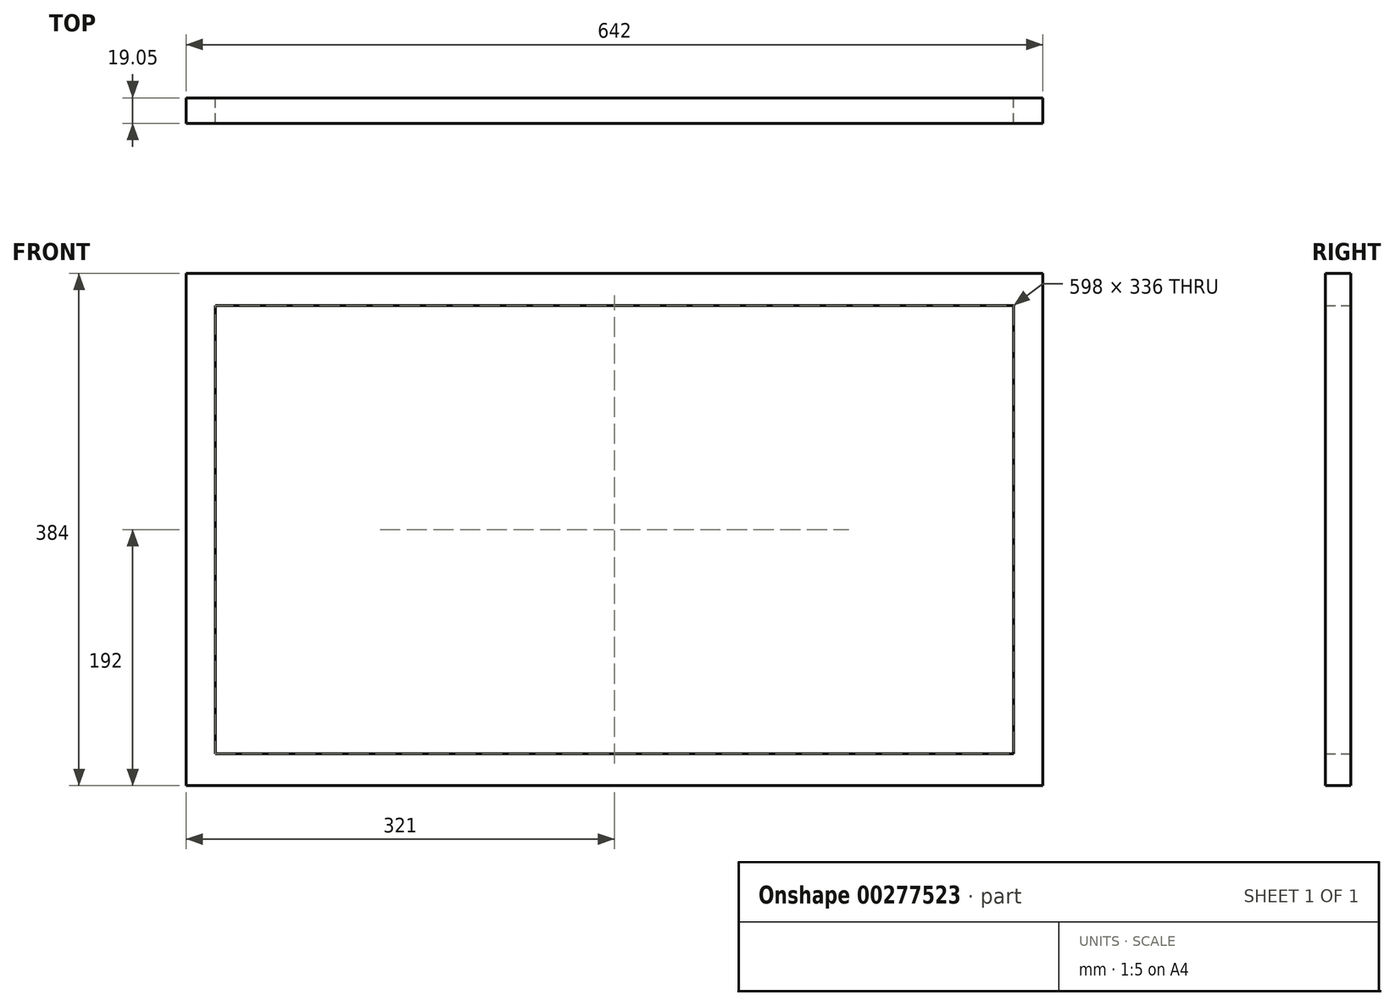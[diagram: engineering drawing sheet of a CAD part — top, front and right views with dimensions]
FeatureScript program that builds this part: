
annotation { "Feature Type Name" : "Feature", "Feature Type Description" : "" }
export const myFeature = defineFeature(function(context is Context, id is Id, definition is map)
    precondition{}
    {
        {
            var Q0;
            Q0=qCreatedBy(makeId("Front.planeOp"),FACE);
            var sketch = newSketch(context, id + "F0", { "sketchPlane" : qUnion([Q0])});
            skLineSegment(sketch, "E0.bottom", {"start": v(-321, 192) * mm, "end": v(321, 192) * mm});
            skLineSegment(sketch, "E0.top", {"start": v(-321, -192) * mm, "end": v(321, -192) * mm});
            skLineSegment(sketch, "E0.left", {"start": v(-321, 192) * mm, "end": v(-321, -192) * mm});
            skLineSegment(sketch, "E0.right", {"start": v(321, 192) * mm, "end": v(321, -192) * mm});
            skPoint(sketch, "E0.middle", {"position": v(0, 0) * mm});
            skSolve(sketch);
        }
        {
            var Q0;
            Q0=makeQuery(id+"F0.imprint","IMPRINT",FACE,{"disambiguationData":[TD([[makeQuery(id+"F0.imprint","IMPRINT",EDGE,{"derivedFrom":sQuery(id+"F0.wireOp",EDGE,"E0.bottom")}),-1.0]])]});
            extrude(context, id + "F1", {"entities" : qUnion([Q0]), "depth" : 19.05 * mm});
        }
        {
            var Q0;
            Q0=qCreatedBy(makeId("Front.planeOp"),FACE);
            var sketch = newSketch(context, id + "F2", { "sketchPlane" : qUnion([Q0])});
            skLineSegment(sketch, "E1.bottom", {"start": v(-299, 168) * mm, "end": v(299, 168) * mm});
            skLineSegment(sketch, "E1.top", {"start": v(-299, -168) * mm, "end": v(299, -168) * mm});
            skLineSegment(sketch, "E1.left", {"start": v(-299, 168) * mm, "end": v(-299, -168) * mm});
            skLineSegment(sketch, "E1.right", {"start": v(299, 168) * mm, "end": v(299, -168) * mm});
            skPoint(sketch, "E1.middle", {"position": v(0, 0) * mm});
            skSolve(sketch);
        }
        {
            var Q0;
            Q0 = qSketchRegion(id + "F2", true);
            extrude(context, id + "F3", {"entities" : qUnion([Q0]), "operationType" : NewBodyOperationType.REMOVE, "depth" : 365.76 * mm});
        }
    });
